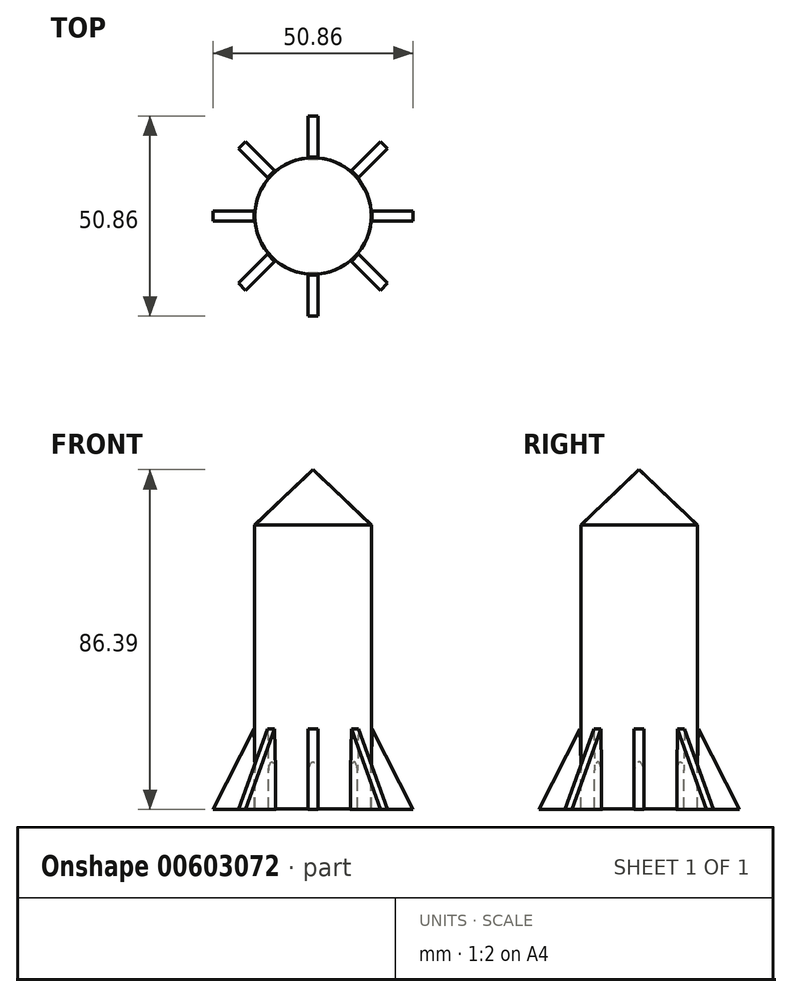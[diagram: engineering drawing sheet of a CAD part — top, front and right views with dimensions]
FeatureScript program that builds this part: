
annotation { "Feature Type Name" : "Feature", "Feature Type Description" : "" }
export const myFeature = defineFeature(function(context is Context, id is Id, definition is map)
    precondition{}
    {
        {
            var Q0;
            Q0=qCreatedBy(makeId("Front.planeOp"),FACE);
            var sketch = newSketch(context, id + "F0", { "sketchPlane" : qUnion([Q0])});
            skLineSegment(sketch, "E0", {"start": v(0, 28.49) * mm, "end": v(0, -43.65) * mm});
            skLineSegment(sketch, "E1", {"start": v(0, 28.49) * mm, "end": v(14.81, 28.49) * mm});
            skLineSegment(sketch, "E2", {"start": v(14.81, 28.49) * mm, "end": v(14.81, -43.65) * mm});
            skLineSegment(sketch, "E3", {"start": v(0, -43.65) * mm, "end": v(14.81, -43.65) * mm});
            skLineSegment(sketch, "E4", {"start": v(0, 42.6) * mm, "end": v(14.81, 28.49) * mm});
            skLineSegment(sketch, "E5", {"start": v(0, 42.6) * mm, "end": v(0, 28.49) * mm});
            skSolve(sketch);
        }
        {
            var Q0;
            Q0=makeQuery(id+"F0.imprint","IMPRINT",FACE,{"disambiguationData":[TD([[makeQuery(id+"F0.imprint","IMPRINT",EDGE,{"derivedFrom":sQuery(id+"F0.wireOp",EDGE,"E0")}),1.0]])]});
            var Q1;
            Q1=makeQuery(id+"F0.imprint","IMPRINT",FACE,{"disambiguationData":[TD([[makeQuery(id+"F0.imprint","IMPRINT",EDGE,{"derivedFrom":sQuery(id+"F0.wireOp",EDGE,"E1")}),1.0]])]});
            var Q2;
            Q2=sQuery(id+"F0.wireOp",EDGE,"E5");
            revolve(context, id + "F1", {"entities" : qUnion([Q0, Q1]), "axis" : qUnion([Q2]), "revolveType" : RevolveType.FULL});
        }
        {
            var Q0;
            Q0=qCreatedBy(makeId("Front.planeOp"),FACE);
            var sketch = newSketch(context, id + "F2", { "sketchPlane" : qUnion([Q0])});
            skLineSegment(sketch, "E6", {"start": v(-14.5, -43.78) * mm, "end": v(-25.43, -43.78) * mm});
            skLineSegment(sketch, "E7", {"start": v(-25.43, -43.78) * mm, "end": v(-15.03, -23.22) * mm});
            skLineSegment(sketch, "E8", {"start": v(-15.03, -23.22) * mm, "end": v(-14.5, -43.78) * mm});
            skSolve(sketch);
        }
        {
            var Q0;
            Q0=makeQuery(id+"F2.imprint","IMPRINT",FACE,{"disambiguationData":[TD([[makeQuery(id+"F2.imprint","IMPRINT",EDGE,{"derivedFrom":sQuery(id+"F2.wireOp",EDGE,"E6")}),-1.0]])]});
            extrude(context, id + "F3", {"entities" : qUnion([Q0]), "operationType" : NewBodyOperationType.ADD, "endBound" : BoundingType.SYMMETRIC, "depth" : 2.54 * mm, "offsetDistance" : 25.4 * mm});
        }
        {
            var Q0;
            Q0=makeQuery(id+"F1.opRevolve","SWEPT_BODY",BODY,{"disambiguationData":[OSD([sQuery(id+"F0.wireOp",EDGE,"E0"),sQuery(id+"F0.wireOp",EDGE,"E2"),sQuery(id+"F0.wireOp",EDGE,"E3"),sQuery(id+"F0.wireOp",EDGE,"E4"),sQuery(id+"F0.wireOp",EDGE,"E5")])]});
            var Q1;
            Q1=makeQuery(id+"F1.opRevolve","SWEPT_FACE",FACE,{"disambiguationData":[OSD([sQuery(id+"F0.wireOp",EDGE,"E2")])]});
            circularPattern(context, id + "F4", {"entities" : qUnion([Q0]), "axis" : qUnion([Q1]), "angle" : 360 * degree, "instanceCount" : 8, "equalSpace" : true});
        }
    });
